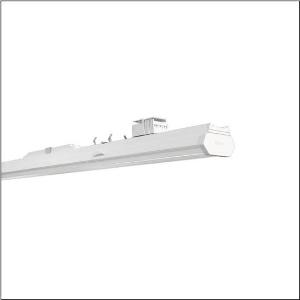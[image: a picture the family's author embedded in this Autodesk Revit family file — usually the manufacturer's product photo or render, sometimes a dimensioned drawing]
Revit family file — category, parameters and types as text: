
# Revit family: licross_r__11_protected_mo_51td11mn495g_5082
name_source: partatom
category: Lighting Fixtures
units: mm (PartAtom-declared; Revit-internal decimal feet)

## family parameters
Cut with Voids When Loaded = No
Host = Face
Light Source = No
Part Type = Normal
Room Calculation Point = No
Round Connector Dimension = Use Diameter
Shared = No

## types (1)
- --- (1 x LED, 9980 lm, 55.3 W, 4000K)
    Apparent Load = 55 VA
    CIE Flux Codes = 83 94 98 100 100
    Color Rendering = 80
    Color Temperature = 4000K
    Default Elevation = 1800 mm
    Description = Licross® 11 Protected MO, luminaire insert, of sheet steel, galvanised, coil coated, white, length: 1.500mm, width: 90mm, height: 101mm, LED rated luminous flux: 9.980lm, light colour: 840, control gear: ON/OFF Multilumen, with plug, 3-pole, with phase selection, mains connection: 220..240V, AC, 50/60Hz, rated input power: 55W, halogen-free wiring, primary light control with lens, of plastic, primary optical cover: cover, of PMMA, light emission: direct distribution, primary light characteristic: symmetric, protection rating (complete): IP54, insulation class (complete): insulation class I (protective earthing), certification: CE, ENEC, VDE, UKCA, protection symbol: D if used in an environment with non-conductive dust loads with corresponding accessories, impact resistance: IK06, permissible ambient temperature for indoor applications: -35..+40°C, corresponds to IFS (International Featured Standards) requirements for safety and quality in the food industry, reducing of maximum allowable ambient temperature of 5°C with ceiling mounting, LABS conformity tested according to VDMA 24364:2018-05, packaging unit: 1 piece
    Height = 92 mm
    Lamp = 1 x LED
    Lamp Light Flux = 9980 lm
    Lamp Power = 55.3 W
    Lamp count = 1
    Length = 1500 mm
    Luminous efficacy = 180 lm/W
    Manufacturer = Siteco
    ModVariant = No
    Model = 51TD11MN495G
    Mounting Place = Ceiling
    Mounting Type = Pendant
    Number of Poles = 1
    OnlyDefault = Yes
    Power Factor = 1
    Product Name = Licross® 11 Protected MO
    Product group = luminaire insert
    ProductGroupID = 901
    Protection Class = Protection class I
    Protection Degree = IP 54
    RLX_Detail_Level = 1
    RLX_Emergency_Light_Flux = 0 lm
    RLX_Emergency_Type = 0
    RLX_Emergency_Type_DB = No
    RlxData = <blob elided: 21797 chars, md5=d446e702>
    Socket = socket
    Standby Power = 0 W
    System Light Flux = 9980 lm
    System Power = 55 W
    Type Comments = factory setting: luminous flux: 100 % | (A | C | E) | 126 mA
    Type Image = l_1256145.jpg
    URL = http://relux.com
    VarID = @adj_019315
    Voltage = 0 V
    Weight = 0.00 kg
    Width = 88 mm

## geometry (parser evidence)
native form markers: Blend x4, Sweep x11
no freeform markers — native parametric forms only
